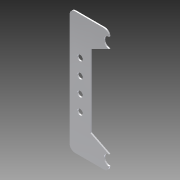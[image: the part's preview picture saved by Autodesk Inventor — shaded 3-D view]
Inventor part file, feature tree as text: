
AUTODESK INVENTOR PART (.ipt)
format: ipt  version: 2014 SP1 (Build 180222100, 222)  size: 117,248 bytes
history: native  units: in
note: dims shown in document units (in); Inventor stores cm internally (conversion verified against a paired STEP export)
features: reference x6, extrude x1, fillet x1, sketch x1
ambient origin geometry x8: Origin, YZ Plane, XZ Plane, XY Plane, X Axis, Y Axis, Z Axis, Center Point
bodies: Solid1 (feature_tree)
feature tree (9):
  extrude  "Extrusion1"  Depth=0.25in
  fillet  "Fillet1"  Radius=0.5in
  sketch  "Sketch1"  dims[d0=3.5in d2=0.5in d3=0.5in d4=0.5in d5=0.5in d6=0.0625in d7=0.0in d8=0.25in]
  reference  "Reference1"
  reference  "Reference2"
  reference  "Reference3"
  reference  "Reference4"
  reference  "Reference5"
  reference  "Reference6"
